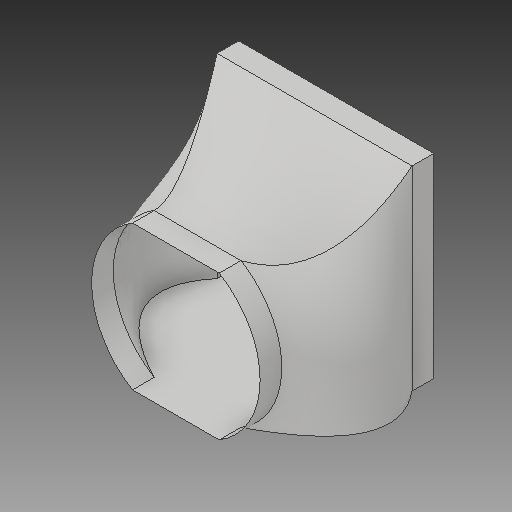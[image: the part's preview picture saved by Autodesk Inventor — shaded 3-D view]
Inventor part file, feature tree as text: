
AUTODESK INVENTOR PART (.ipt)
format: ipt  version: 2017 (Build 210142000, 142)  size: 334,336 bytes
history: native  units: in
note: dims shown in document units (in); Inventor stores cm internally (conversion verified against a paired STEP export)
features: extrude x2, other x2, sketch x2, loft x2, delete_face x1
ambient origin geometry x8: Origin, YZ Plane, XZ Plane, XY Plane, X Axis, Y Axis, Z Axis, Center Point
bodies: Solid1 (feature_tree)
feature tree (9):
  extrude  "connection"  Depth=2.7in
  other  "front half of room"
  other  "front of room"
  sketch  "Sketch3"  dims[d12=1.0in d13=0.0in d14=2.7in]
  loft  "shell make "
  loft  "shell cut"
  extrude  "connection to door"  Depth=9.0in
  delete_face  "Delete Face3"
  sketch  "Sketch5"  dims[d17=2.7in d26=69.0in d27=59.0in d33=1.0in d34=1.0in d35=1.0in d36=1.0in d153=6.21in d154=5.31in d157=0.0in d158=90.0deg d159=0.0in d160=90.0deg d161=0.0in d162=90.0deg d180=0.0in d181=90.0deg d182=0.0in d183=90.0deg d184=0.0in d185=90.0deg d217=3.082in d219=1.0in d220=1.0in d221=9.0in d222=9.0in d223=1.0in d241=1.0in d242=1.0in d243=1.0in d244=1.0in d245=1.0in d246=0.0in d262=4.0in d263=1.0in d264=4.8944in d266=3.8873in d267=3.8873in d271=1.6458in]
